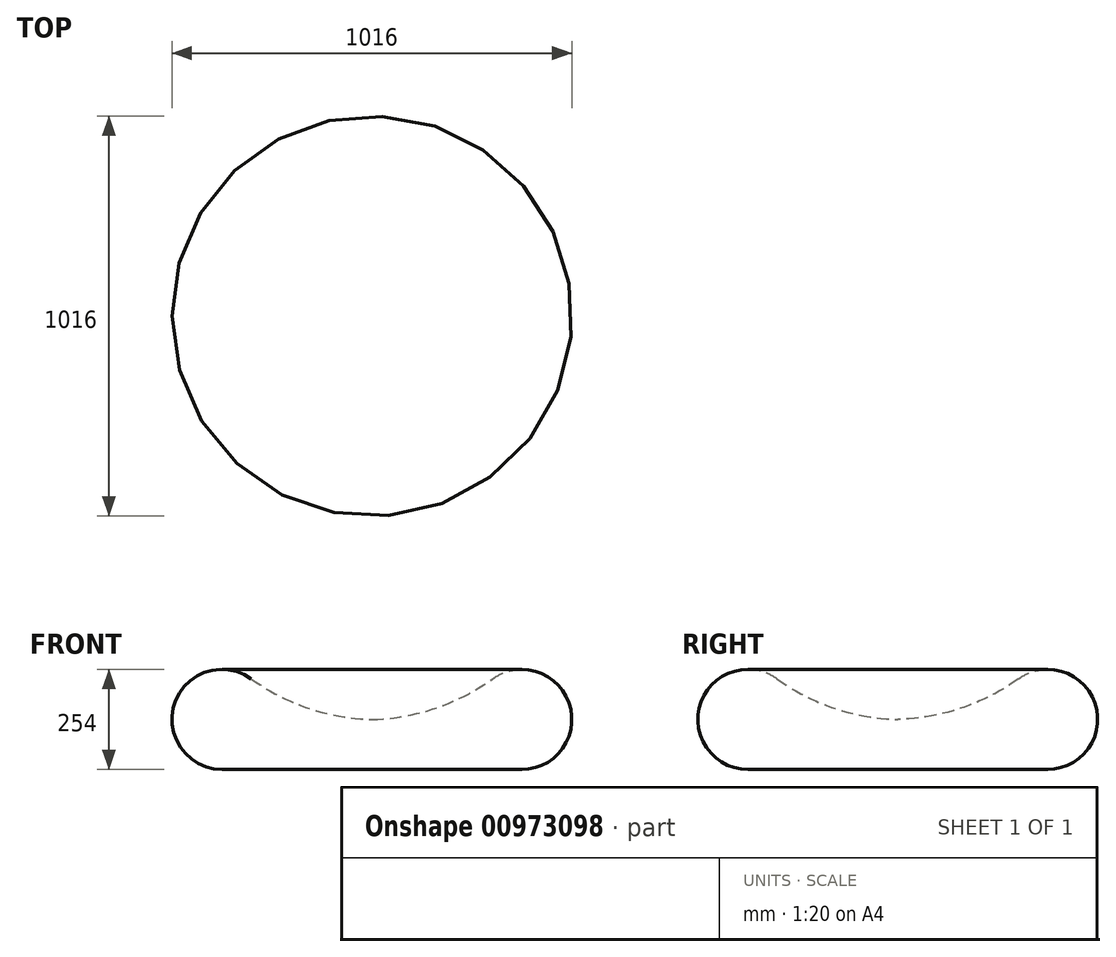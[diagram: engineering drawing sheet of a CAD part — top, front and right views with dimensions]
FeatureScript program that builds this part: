
annotation { "Feature Type Name" : "Feature", "Feature Type Description" : "" }
export const myFeature = defineFeature(function(context is Context, id is Id, definition is map)
    precondition{}
    {
        {
            var Q0;
            Q0=qCreatedBy(makeId("Front.planeOp"),FACE);
            var sketch = newSketch(context, id + "F0", { "sketchPlane" : qUnion([Q0])});
            skArc(sketch, "E0", {"start": v(-307.02, 230.23) * mm, "mid": v(-501.91, 165.85) * mm, "end": v(-381, 0) * mm});
            skArc(sketch, "E1", {"start": v(-307.02, 230.23) * mm, "mid": v(-161.25, 155.62) * mm, "end": v(0, 127) * mm});
            skLineSegment(sketch, "E2", {"start": v(0, 0) * mm, "end": v(-381, 0) * mm});
            skLineSegment(sketch, "E3", {"start": v(-381, 0) * mm, "end": v(0, 0) * mm});
            skLineSegment(sketch, "E4", {"start": v(0, 0) * mm, "end": v(0, 127) * mm});
            skLineSegment(sketch, "E5", {"start": v(0, 127) * mm, "end": v(0, 0) * mm});
            skSolve(sketch);
        }
        {
            var Q0;
            Q0 = qSketchRegion(id + "F0", true);
            var Q1;
            Q1=sQuery(id+"F0.wireOp",EDGE,"E0");
            var Q2;
            Q2=sQuery(id+"F0.wireOp",EDGE,"E1");
            var Q3;
            Q3=sQuery(id+"F0.wireOp",EDGE,"E3");
            var Q4;
            Q4=sQuery(id+"F0.wireOp",EDGE,"E5");
            revolve(context, id + "F1", {"bodyType" : ToolBodyType.SURFACE, "surfaceOperationType" : NewSurfaceOperationType.NEW, "entities" : qUnion([Q0]), "surfaceEntities" : qUnion([Q1, Q2, Q3]), "axis" : qUnion([Q4]), "revolveType" : RevolveType.FULL});
        }
    });
